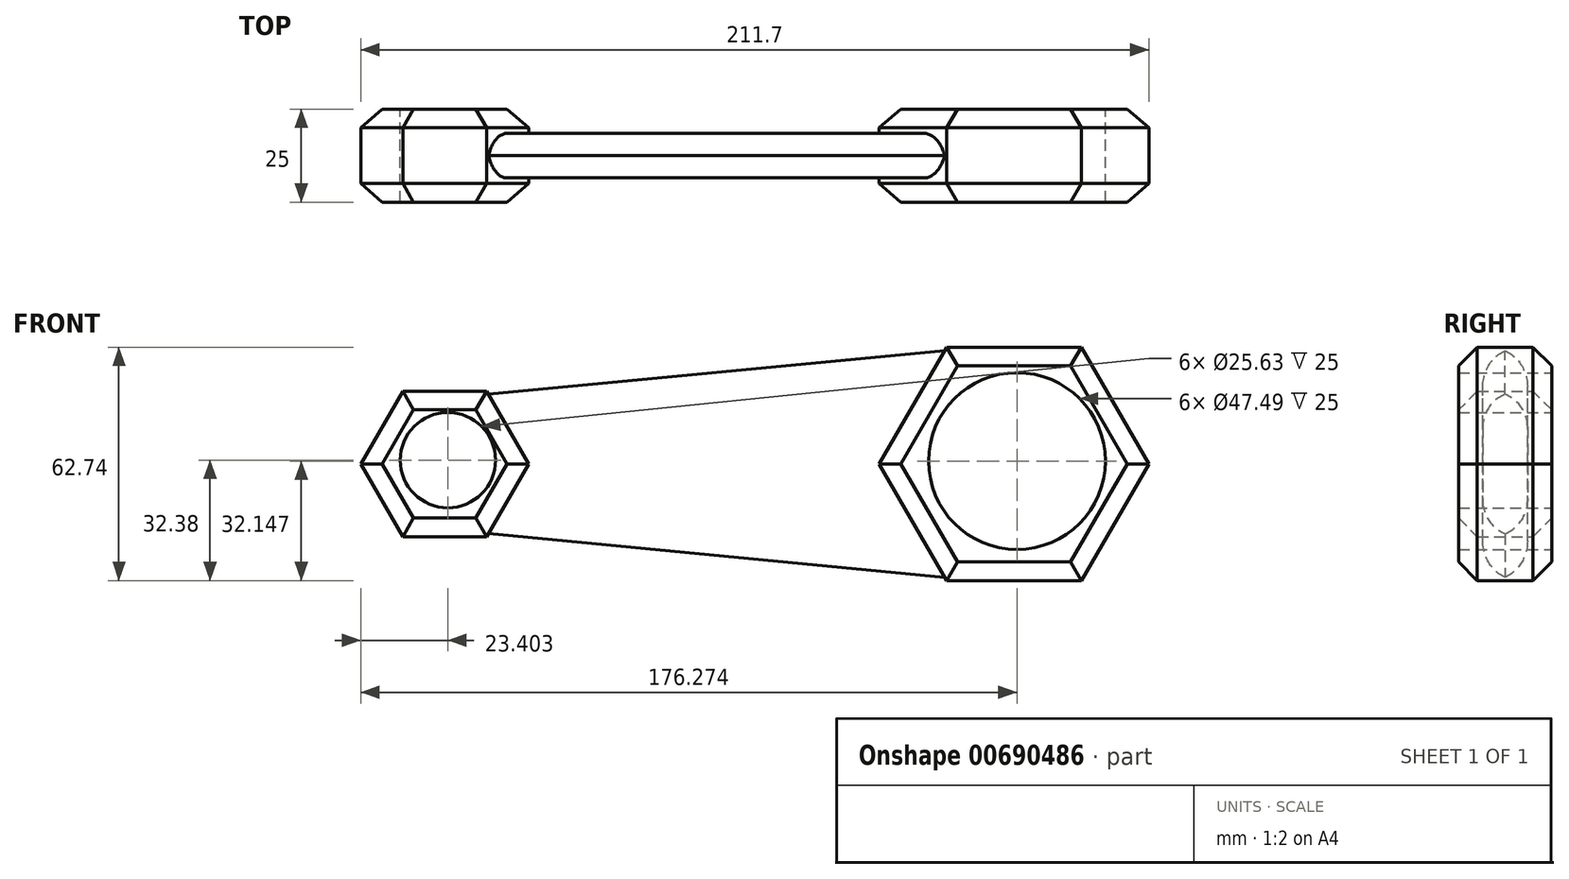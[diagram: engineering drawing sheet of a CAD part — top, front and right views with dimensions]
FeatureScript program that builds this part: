
annotation { "Feature Type Name" : "Feature", "Feature Type Description" : "" }
export const myFeature = defineFeature(function(context is Context, id is Id, definition is map)
    precondition{}
    {
        {
            var Q0;
            Q0=qCreatedBy(makeId("Front.planeOp"),FACE);
            var sketch = newSketch(context, id + "F0", { "sketchPlane" : qUnion([Q0])});
            skCircle(sketch, "E0.cCircle", {"center": v(0, 0) * mm, "radius": 31.37 * mm, "construction": true});
            skLineSegment(sketch, "E0.0", {"start": v(-18.11, 31.37) * mm, "end": v(18.11, 31.37) * mm});
            skLineSegment(sketch, "E0.1", {"start": v(18.11, 31.37) * mm, "end": v(36.23, 0) * mm});
            skLineSegment(sketch, "E0.2", {"start": v(36.23, 0) * mm, "end": v(18.11, -31.37) * mm});
            skLineSegment(sketch, "E0.3", {"start": v(18.11, -31.37) * mm, "end": v(-18.11, -31.37) * mm});
            skLineSegment(sketch, "E0.4", {"start": v(-18.11, -31.37) * mm, "end": v(-36.23, 0) * mm});
            skLineSegment(sketch, "E0.5", {"start": v(-36.23, 0) * mm, "end": v(-18.11, 31.37) * mm});
            skPoint(sketch, "E0.0.midPoint", {"position": v(0, 31.37) * mm});
            skCircle(sketch, "E1.cCircle", {"center": v(-152.92, 0) * mm, "radius": 19.53 * mm, "construction": true});
            skLineSegment(sketch, "E1.0", {"start": v(-164.2, 19.53) * mm, "end": v(-141.65, 19.53) * mm});
            skLineSegment(sketch, "E1.1", {"start": v(-141.65, 19.53) * mm, "end": v(-130.37, 0) * mm});
            skLineSegment(sketch, "E1.2", {"start": v(-130.37, 0) * mm, "end": v(-141.65, -19.53) * mm});
            skLineSegment(sketch, "E1.3", {"start": v(-141.65, -19.53) * mm, "end": v(-164.2, -19.53) * mm});
            skLineSegment(sketch, "E1.4", {"start": v(-164.2, -19.53) * mm, "end": v(-175.47, 0) * mm});
            skLineSegment(sketch, "E1.5", {"start": v(-175.47, 0) * mm, "end": v(-164.2, 19.53) * mm});
            skPoint(sketch, "E1.0.midPoint", {"position": v(-152.92, 19.53) * mm});
            skLineSegment(sketch, "E2", {"start": v(-141.65, 19.53) * mm, "end": v(-18.11, 31.37) * mm});
            skLineSegment(sketch, "E3", {"start": v(-18.11, -31.37) * mm, "end": v(-141.65, -19.53) * mm});
            skSolve(sketch);
        }
        {
            var Q0;
            Q0=makeQuery(id+"F0.imprint","IMPRINT",FACE,{"disambiguationData":[TD([[makeQuery(id+"F0.imprint","IMPRINT",EDGE,{"derivedFrom":sQuery(id+"F0.wireOp",EDGE,"E0.0")}),-1.0]])]});
            extrude(context, id + "F1", {"entities" : qUnion([Q0]), "endBound" : BoundingType.SYMMETRIC, "depth" : 25 * mm, "offsetDistance" : 25 * mm});
        }
        {
            var Q0;
            Q0=makeQuery(id+"F0.imprint","IMPRINT",FACE,{"disambiguationData":[TD([[makeQuery(id+"F0.imprint","IMPRINT",EDGE,{"derivedFrom":sQuery(id+"F0.wireOp",EDGE,"E1.0")}),-1.0]])]});
            extrude(context, id + "F2", {"entities" : qUnion([Q0]), "endBound" : BoundingType.SYMMETRIC, "depth" : 25 * mm, "offsetDistance" : 25 * mm});
        }
        {
            var Q0;
            Q0=makeQuery(id+"F0.imprint","IMPRINT",FACE,{"disambiguationData":[TD([[makeQuery(id+"F0.imprint","IMPRINT",EDGE,{"derivedFrom":sQuery(id+"F0.wireOp",EDGE,"E0.4")}),1.0]])]});
            extrude(context, id + "F3", {"entities" : qUnion([Q0]), "endBound" : BoundingType.SYMMETRIC, "depth" : 12 * mm, "offsetDistance" : 25 * mm});
        }
        {
            var Q0;
            Q0=makeQuery(id+"F1.opExtrude","CAP_FACE",FACE,{"disambiguationData":[OSD([sQuery(id+"F0.wireOp",EDGE,"E0.0"),sQuery(id+"F0.wireOp",EDGE,"E0.1"),sQuery(id+"F0.wireOp",EDGE,"E0.2"),sQuery(id+"F0.wireOp",EDGE,"E0.3"),sQuery(id+"F0.wireOp",EDGE,"E0.4"),sQuery(id+"F0.wireOp",EDGE,"E0.5")])],"isStart":false});
            var sketch = newSketch(context, id + "F4", { "sketchPlane" : qUnion([Q0])});
            skCircle(sketch, "E4", {"center": v(0.8, 0.78) * mm, "radius": 23.75 * mm});
            skSolve(sketch);
        }
        {
            var Q0;
            Q0=makeQuery(id+"F2.opExtrude","CAP_FACE",FACE,{"disambiguationData":[OSD([sQuery(id+"F0.wireOp",EDGE,"E1.0"),sQuery(id+"F0.wireOp",EDGE,"E1.1"),sQuery(id+"F0.wireOp",EDGE,"E1.2"),sQuery(id+"F0.wireOp",EDGE,"E1.3"),sQuery(id+"F0.wireOp",EDGE,"E1.4"),sQuery(id+"F0.wireOp",EDGE,"E1.5")])],"isStart":false});
            var sketch = newSketch(context, id + "F5", { "sketchPlane" : qUnion([Q0])});
            skCircle(sketch, "E5", {"center": v(-152.07, 1.01) * mm, "radius": 12.81 * mm});
            skSolve(sketch);
        }
        {
            var Q0;
            Q0=makeQuery(id+"F5.imprint","IMPRINT",FACE,{"disambiguationData":[TD([[makeQuery(id+"F5.imprint","IMPRINT",EDGE,{"derivedFrom":sQuery(id+"F5.wireOp",EDGE,"E5")}),1.0]])]});
            var Q1;
            Q1=makeQuery(id+"F2.opExtrude","SWEPT_EDGE",EDGE,{"disambiguationData":[OSD([sQuery(id+"F0.wireOp",EDGE,"E1.0"),sQuery(id+"F0.wireOp",EDGE,"E1.5")])]});
            sweep(context, id + "F6", {"operationType" : NewBodyOperationType.REMOVE, "profiles" : qUnion([Q0]), "path" : qUnion([Q1])});
        }
        {
            var Q0;
            Q0=makeQuery(id+"F4.imprint","IMPRINT",FACE,{"disambiguationData":[TD([[makeQuery(id+"F4.imprint","IMPRINT",EDGE,{"derivedFrom":sQuery(id+"F4.wireOp",EDGE,"E4")}),1.0]])]});
            var Q1;
            Q1=makeQuery(id+"F1.opExtrude","SWEPT_EDGE",EDGE,{"disambiguationData":[OSD([sQuery(id+"F0.wireOp",EDGE,"E0.2"),sQuery(id+"F0.wireOp",EDGE,"E0.3")])]});
            sweep(context, id + "F7", {"operationType" : NewBodyOperationType.REMOVE, "profiles" : qUnion([Q0]), "path" : qUnion([Q1])});
        }
        {
            var Q0;
            Q0=makeQuery(id+"F3.opExtrude","CAP_EDGE",EDGE,{"disambiguationData":[OSD([sQuery(id+"F0.wireOp",EDGE,"E3")])],"isStart":true});
            var Q1;
            Q1=makeQuery(id+"F3.opExtrude","CAP_EDGE",EDGE,{"disambiguationData":[OSD([sQuery(id+"F0.wireOp",EDGE,"E3")])],"isStart":false});
            var Q2;
            Q2=makeQuery(id+"F3.opExtrude","CAP_EDGE",EDGE,{"disambiguationData":[OSD([sQuery(id+"F0.wireOp",EDGE,"E2")])],"isStart":false});
            var Q3;
            Q3=makeQuery(id+"F3.opExtrude","CAP_EDGE",EDGE,{"disambiguationData":[OSD([sQuery(id+"F0.wireOp",EDGE,"E2")])],"isStart":true});
            fillet(context, id + "F8", {"entities" : qUnion([Q0, Q1, Q2, Q3]), "radius" : 10 * mm, "tangentPropagation" : true, "allowEdgeOverflow" : false});
        }
        {
            var Q0;
            Q0=makeQuery(id+"F2.opExtrude","CAP_EDGE",EDGE,{"disambiguationData":[OSD([sQuery(id+"F0.wireOp",EDGE,"E1.3")])],"isStart":false});
            var Q1;
            Q1=makeQuery(id+"F2.opExtrude","CAP_EDGE",EDGE,{"disambiguationData":[OSD([sQuery(id+"F0.wireOp",EDGE,"E1.4")])],"isStart":false});
            var Q2;
            Q2=makeQuery(id+"F2.opExtrude","CAP_EDGE",EDGE,{"disambiguationData":[OSD([sQuery(id+"F0.wireOp",EDGE,"E1.5")])],"isStart":false});
            var Q3;
            Q3=makeQuery(id+"F2.opExtrude","CAP_EDGE",EDGE,{"disambiguationData":[OSD([sQuery(id+"F0.wireOp",EDGE,"E1.0")])],"isStart":false});
            var Q4;
            Q4=makeQuery(id+"F2.opExtrude","CAP_EDGE",EDGE,{"disambiguationData":[OSD([sQuery(id+"F0.wireOp",EDGE,"E1.2")])],"isStart":false});
            var Q5;
            Q5=makeQuery(id+"F2.opExtrude","CAP_EDGE",EDGE,{"disambiguationData":[OSD([sQuery(id+"F0.wireOp",EDGE,"E1.1")])],"isStart":false});
            var Q6;
            Q6=makeQuery(id+"F1.opExtrude","CAP_EDGE",EDGE,{"disambiguationData":[OSD([sQuery(id+"F0.wireOp",EDGE,"E0.2")])],"isStart":false});
            var Q7;
            Q7=makeQuery(id+"F1.opExtrude","CAP_EDGE",EDGE,{"disambiguationData":[OSD([sQuery(id+"F0.wireOp",EDGE,"E0.3")])],"isStart":false});
            var Q8;
            Q8=makeQuery(id+"F1.opExtrude","CAP_EDGE",EDGE,{"disambiguationData":[OSD([sQuery(id+"F0.wireOp",EDGE,"E0.4")])],"isStart":false});
            var Q9;
            Q9=makeQuery(id+"F1.opExtrude","CAP_EDGE",EDGE,{"disambiguationData":[OSD([sQuery(id+"F0.wireOp",EDGE,"E0.5")])],"isStart":false});
            var Q10;
            Q10=makeQuery(id+"F1.opExtrude","CAP_EDGE",EDGE,{"disambiguationData":[OSD([sQuery(id+"F0.wireOp",EDGE,"E0.0")])],"isStart":false});
            var Q11;
            Q11=makeQuery(id+"F1.opExtrude","CAP_EDGE",EDGE,{"disambiguationData":[OSD([sQuery(id+"F0.wireOp",EDGE,"E0.1")])],"isStart":false});
            var Q12;
            Q12=makeQuery(id+"F1.opExtrude","CAP_EDGE",EDGE,{"disambiguationData":[OSD([sQuery(id+"F0.wireOp",EDGE,"E0.1")])],"isStart":true});
            var Q13;
            Q13=makeQuery(id+"F1.opExtrude","CAP_EDGE",EDGE,{"disambiguationData":[OSD([sQuery(id+"F0.wireOp",EDGE,"E0.2")])],"isStart":true});
            var Q14;
            Q14=makeQuery(id+"F1.opExtrude","CAP_EDGE",EDGE,{"disambiguationData":[OSD([sQuery(id+"F0.wireOp",EDGE,"E0.0")])],"isStart":true});
            var Q15;
            Q15=makeQuery(id+"F1.opExtrude","CAP_EDGE",EDGE,{"disambiguationData":[OSD([sQuery(id+"F0.wireOp",EDGE,"E0.5")])],"isStart":true});
            var Q16;
            Q16=makeQuery(id+"F1.opExtrude","CAP_EDGE",EDGE,{"disambiguationData":[OSD([sQuery(id+"F0.wireOp",EDGE,"E0.4")])],"isStart":true});
            var Q17;
            Q17=makeQuery(id+"F1.opExtrude","CAP_EDGE",EDGE,{"disambiguationData":[OSD([sQuery(id+"F0.wireOp",EDGE,"E0.3")])],"isStart":true});
            var Q18;
            Q18=makeQuery(id+"F2.opExtrude","CAP_EDGE",EDGE,{"disambiguationData":[OSD([sQuery(id+"F0.wireOp",EDGE,"E1.3")])],"isStart":true});
            var Q19;
            Q19=makeQuery(id+"F2.opExtrude","CAP_EDGE",EDGE,{"disambiguationData":[OSD([sQuery(id+"F0.wireOp",EDGE,"E1.4")])],"isStart":true});
            var Q20;
            Q20=makeQuery(id+"F2.opExtrude","CAP_EDGE",EDGE,{"disambiguationData":[OSD([sQuery(id+"F0.wireOp",EDGE,"E1.5")])],"isStart":true});
            var Q21;
            Q21=makeQuery(id+"F2.opExtrude","CAP_EDGE",EDGE,{"disambiguationData":[OSD([sQuery(id+"F0.wireOp",EDGE,"E1.0")])],"isStart":true});
            var Q22;
            Q22=makeQuery(id+"F2.opExtrude","CAP_EDGE",EDGE,{"disambiguationData":[OSD([sQuery(id+"F0.wireOp",EDGE,"E1.1")])],"isStart":true});
            var Q23;
            Q23=makeQuery(id+"F2.opExtrude","CAP_EDGE",EDGE,{"disambiguationData":[OSD([sQuery(id+"F0.wireOp",EDGE,"E1.2")])],"isStart":true});
            chamfer(context, id + "F9", {"entities" : qUnion([Q0, Q1, Q2, Q3, Q4, Q5, Q6, Q7, Q8, Q9, Q10, Q11, Q12, Q13, Q14, Q15, Q16, Q17, Q18, Q19, Q20, Q21, Q22, Q23]), "width" : 5 * mm, "tangentPropagation" : true});
        }
    });
